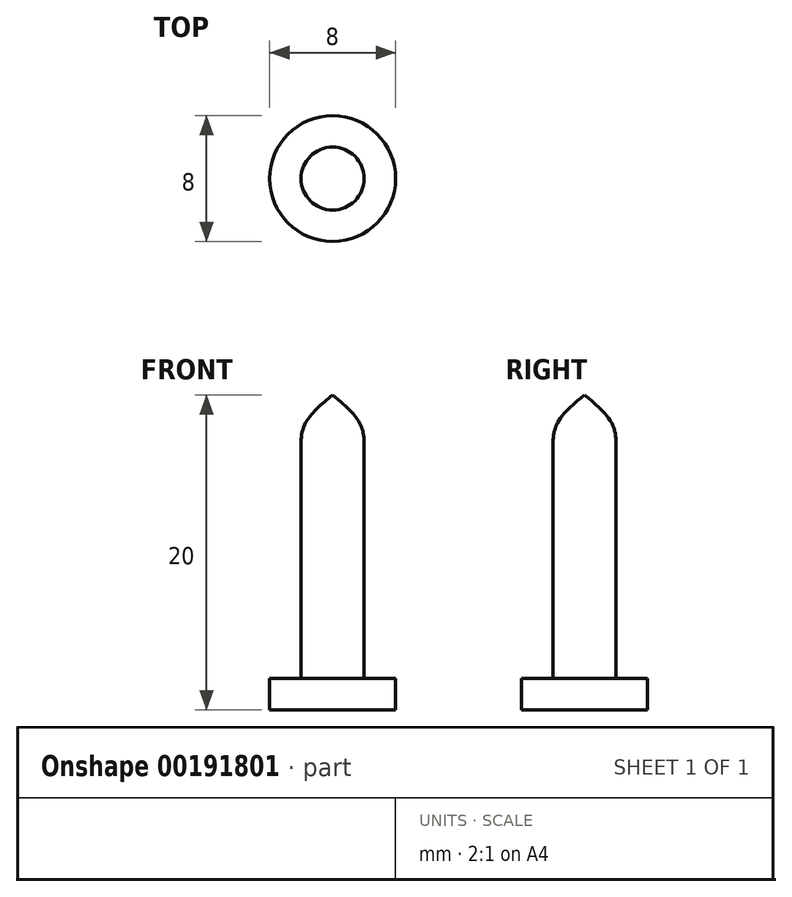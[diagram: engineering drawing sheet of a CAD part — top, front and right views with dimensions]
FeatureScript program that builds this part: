
annotation { "Feature Type Name" : "Feature", "Feature Type Description" : "" }
export const myFeature = defineFeature(function(context is Context, id is Id, definition is map)
    precondition{}
    {
        {
            var Q0;
            Q0=qCreatedBy(makeId("Top.planeOp"),FACE);
            var sketch = newSketch(context, id + "F0", { "sketchPlane" : qUnion([Q0])});
            skCircle(sketch, "E0", {"center": v(0, 0) * mm, "radius": 2 * mm});
            skCircle(sketch, "E1", {"center": v(0, 0) * mm, "radius": 4 * mm});
            skSolve(sketch);
        }
        {
            var Q0;
            Q0=makeQuery(id+"F0.imprint","IMPRINT",FACE,{"disambiguationData":[TD([[makeQuery(id+"F0.imprint","IMPRINT",EDGE,{"derivedFrom":sQuery(id+"F0.wireOp",EDGE,"E0")}),-1.0]])]});
            var Q1;
            Q1=makeQuery(id+"F0.imprint","IMPRINT",FACE,{"disambiguationData":[TD([[makeQuery(id+"F0.imprint","IMPRINT",EDGE,{"derivedFrom":sQuery(id+"F0.wireOp",EDGE,"E0")}),1.0]])]});
            extrude(context, id + "F1", {"entities" : qUnion([Q0, Q1]), "depth" : 2 * mm});
        }
        {
            var Q0;
            Q0=qCreatedBy(makeId("Front.planeOp"),FACE);
            var sketch = newSketch(context, id + "F2", { "sketchPlane" : qUnion([Q0])});
            skLineSegment(sketch, "E2", {"start": v(0, 0) * mm, "end": v(2, 0) * mm});
            skLineSegment(sketch, "E3", {"start": v(2, 0) * mm, "end": v(2, 17) * mm});
            skLineSegment(sketch, "E4", {"start": v(2, 17) * mm, "end": v(0, 20) * mm});
            skLineSegment(sketch, "E5", {"start": v(0, 20) * mm, "end": v(0, 0) * mm});
            skFitSpline(sketch, "E6", {"points": [v(0, 20) * mm, v(2, 17) * mm], "startDerivative": vector(4.3, -3.52) * mm, "endDerivative": vector(0.02, -3.68) * mm});
            skSolve(sketch);
        }
        {
            var Q0;
            Q0=makeQuery(id+"F2.imprint","IMPRINT",FACE,{"disambiguationData":[TD([[makeQuery(id+"F2.imprint","IMPRINT",EDGE,{"derivedFrom":sQuery(id+"F2.wireOp",EDGE,"E4")}),-1.0]])]});
            var Q1;
            Q1=makeQuery(id+"F2.imprint","IMPRINT",FACE,{"disambiguationData":[TD([[makeQuery(id+"F2.imprint","IMPRINT",EDGE,{"derivedFrom":sQuery(id+"F2.wireOp",EDGE,"E2")}),1.0]])]});
            var Q2;
            Q2=sQuery(id+"F2.wireOp",EDGE,"E5");
            revolve(context, id + "F3", {"operationType" : NewBodyOperationType.ADD, "entities" : qUnion([Q0, Q1]), "axis" : qUnion([Q2]), "revolveType" : RevolveType.FULL});
        }
    });
